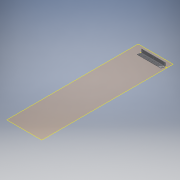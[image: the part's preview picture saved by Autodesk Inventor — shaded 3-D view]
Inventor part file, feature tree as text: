
AUTODESK INVENTOR PART (.ipt)
format: ipt  version: 2016 (Build 200138000, 138)  size: 159,232 bytes
history: native  units: mm
features: sheet_metal_op x4, sketch x3, plane x2, other x2, hole x1, reference x1, projected_geometry x1
ambient origin geometry x8: Origin, YZ Plane, XZ Plane, XY Plane, X Axis, Y Axis, Z Axis, Center Point
bodies: Solid1 (feature_tree)
feature tree (14):
  plane  "Work Plane1"
  sheet_metal_op  "Face1"
  plane  "Work Plane2"
  sheet_metal_op  "Flange1"
  hole  "Hole1"  [1 undecoded]
  sketch  "Sketch1"  dims[d0=5.0mm d2=5.0mm]
  reference  "Reference1"
  other  "Plate1"
  sketch  "Sketch3"  dims[d3=2.5mm]
  other  "Plate2"
  sheet_metal_op  "Bend1"
  sheet_metal_op  "Corner1"
  sketch  "Sketch4"  dims[d4=10.0mm d5=5.0mm d6=50.0mm d7=90.0deg d8=5.0mm d9=20.0mm d10=5.0mm d11=5.0mm d12=48.0mm d13=12.0mm d14=6.2mm d15=6.0mm d16=4.0mm d17=2.0mm d18=90.0deg d19=5.0mm d20=20.594885mm]
  projected_geometry  "Projected Loop1"
note: 1 required parameter value undecoded (feature->parameter linkage not recoverable at this tier; creation-order binding heuristic only, values carry confidence <= 0.55)
